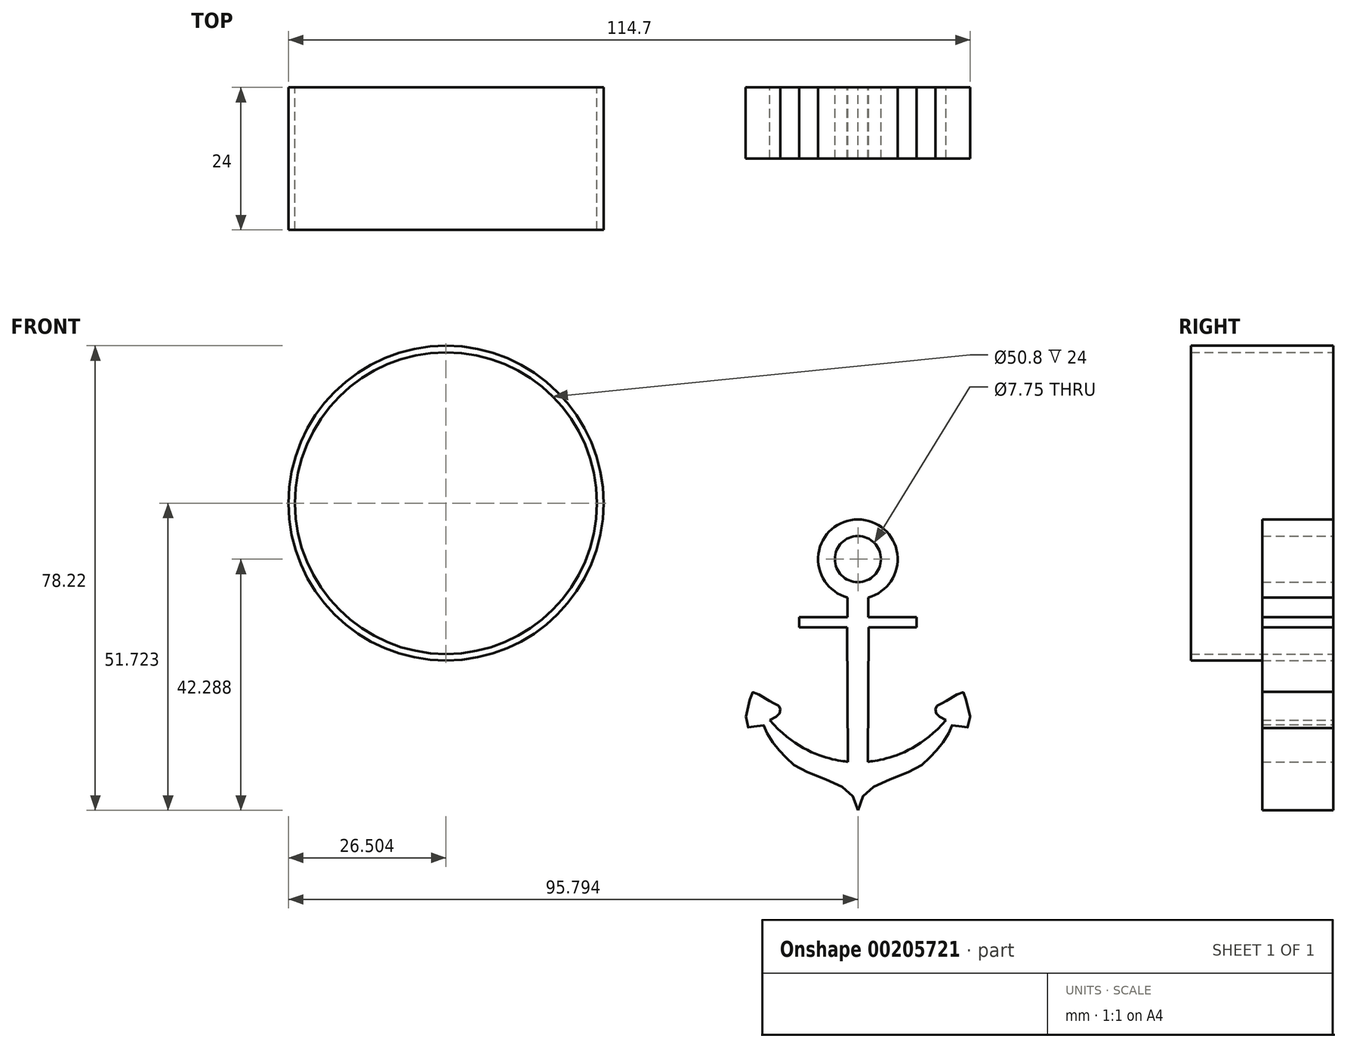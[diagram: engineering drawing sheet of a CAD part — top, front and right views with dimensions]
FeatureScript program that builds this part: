
annotation { "Feature Type Name" : "Feature", "Feature Type Description" : "" }
export const myFeature = defineFeature(function(context is Context, id is Id, definition is map)
    precondition{}
    {
        {
            var Q0;
            Q0=qCreatedBy(makeId("Front.planeOp"),FACE);
            var sketch = newSketch(context, id + "F0", { "sketchPlane" : qUnion([Q0])});
            skCircle(sketch, "E0", {"center": v(-23.28, 15.3) * mm, "radius": 3.88 * mm});
            skArc(sketch, "E1", {"start": v(-21.53, 8.85) * mm, "mid": v(-23.28, 22) * mm, "end": v(-25.02, 8.85) * mm});
            skLineSegment(sketch, "E2", {"start": v(-25.02, 8.85) * mm, "end": v(-25.02, 5.56) * mm});
            skLineSegment(sketch, "E3", {"start": v(-25.02, 5.56) * mm, "end": v(-33.15, 5.56) * mm});
            skLineSegment(sketch, "E4", {"start": v(-33.15, 5.56) * mm, "end": v(-33.15, 3.81) * mm});
            skLineSegment(sketch, "E5", {"start": v(-33.15, 3.81) * mm, "end": v(-25.07, 3.81) * mm});
            skLineSegment(sketch, "E6", {"start": v(-25.07, 3.81) * mm, "end": v(-24.97, -18.82) * mm});
            skFitSpline(sketch, "E7", {"points": [v(-24.97, -18.82) * mm, v(-38.12, -11.75) * mm], "startDerivative": vector(-4.77, 0.72) * mm, "endDerivative": vector(-15.97, 18.98) * mm});
            skFitSpline(sketch, "E8", {"points": [v(-38.12, -11.75) * mm, v(-38.12, -11.77) * mm, v(-37.22, -11.31) * mm, v(-36.63, -10.9) * mm, v(-36.4, -10.53) * mm, v(-36.3, -10.07) * mm, v(-36.42, -9.64) * mm, v(-36.56, -9.43) * mm, v(-36.88, -9.2) * mm, v(-37.57, -8.88) * mm, v(-38.44, -8.4) * mm, v(-40.95, -7.04) * mm, v(-41, -7.09) * mm, v(-41.08, -7.29) * mm, v(-42.14, -12.38) * mm, v(-40.97, -13.09) * mm, v(-39.27, -12.55) * mm, v(-38.6, -13.87) * mm, v(-37.17, -16.1) * mm, v(-35.64, -17.8) * mm, v(-33.21, -19.87) * mm, v(-25.9, -23.03) * mm, v(-23.27, -27) * mm], "startDerivative": vector(-3.71, 10.28) * mm, "endDerivative": vector(10.29, -66.24) * mm});
            skLineSegment(sketch, "E9", {"start": v(-23.28, 15.3) * mm, "end": v(-23.28, 12.34) * mm, "construction": true});
            skLineSegment(sketch, "E10.MirrorCS", {"start": v(-21.53, 8.85) * mm, "end": v(-21.53, 5.56) * mm});
            skLineSegment(sketch, "E11.MirrorCS", {"start": v(-13.4, 5.56) * mm, "end": v(-13.4, 3.81) * mm});
            skFitSpline(sketch, "E12.MirrorCS", {"points": [v(-8.43, -11.75) * mm, v(-8.43, -11.77) * mm, v(-9.33, -11.31) * mm, v(-9.92, -10.9) * mm, v(-10.16, -10.53) * mm, v(-10.25, -10.07) * mm, v(-10.13, -9.64) * mm, v(-9.99, -9.43) * mm, v(-9.67, -9.2) * mm, v(-8.99, -8.88) * mm, v(-8.12, -8.4) * mm, v(-5.6, -7.04) * mm, v(-5.56, -7.09) * mm, v(-5.47, -7.29) * mm, v(-4.41, -12.38) * mm, v(-5.58, -13.09) * mm, v(-7.28, -12.55) * mm, v(-7.96, -13.87) * mm, v(-9.38, -16.1) * mm, v(-10.9, -17.8) * mm, v(-13.34, -19.87) * mm, v(-20.64, -23.03) * mm, v(-23.28, -27) * mm], "startDerivative": vector(3.71, 10.28) * mm, "endDerivative": vector(-10.29, -66.24) * mm});
            skFitSpline(sketch, "E13.MirrorCS", {"points": [v(-21.58, -18.82) * mm, v(-8.43, -11.75) * mm], "startDerivative": vector(4.77, 0.72) * mm, "endDerivative": vector(15.97, 18.98) * mm});
            skLineSegment(sketch, "E14.MirrorCS", {"start": v(-21.53, 5.56) * mm, "end": v(-13.4, 5.56) * mm});
            skLineSegment(sketch, "E15.MirrorCS", {"start": v(-13.4, 3.81) * mm, "end": v(-21.49, 3.81) * mm});
            skLineSegment(sketch, "E16.MirrorCS", {"start": v(-21.49, 3.81) * mm, "end": v(-21.58, -18.82) * mm});
            skPoint(sketch, "E17.center.orphan", {"position": v(-72.77, 0) * mm});
            skSolve(sketch);
        }
        {
            var Q0;
            Q0 = qSketchRegion(id + "F0", true);
            extrude(context, id + "F1", {"entities" : qUnion([Q0]), "depth" : 12 * mm});
        }
        {
            var Q0;
            Q0=qCreatedBy(makeId("Front.planeOp"),FACE);
            var sketch = newSketch(context, id + "F2", { "sketchPlane" : qUnion([Q0])});
            skCircle(sketch, "E18", {"center": v(-92.57, 24.74) * mm, "radius": 25.4 * mm});
            skCircle(sketch, "E19", {"center": v(-92.57, 24.74) * mm, "radius": 26.5 * mm});
            skSolve(sketch);
        }
        {
            var Q0;
            Q0 = qSketchRegion(id + "F2", true);
            extrude(context, id + "F3", {"entities" : qUnion([Q0]), "depth" : 24 * mm});
        }
    });
